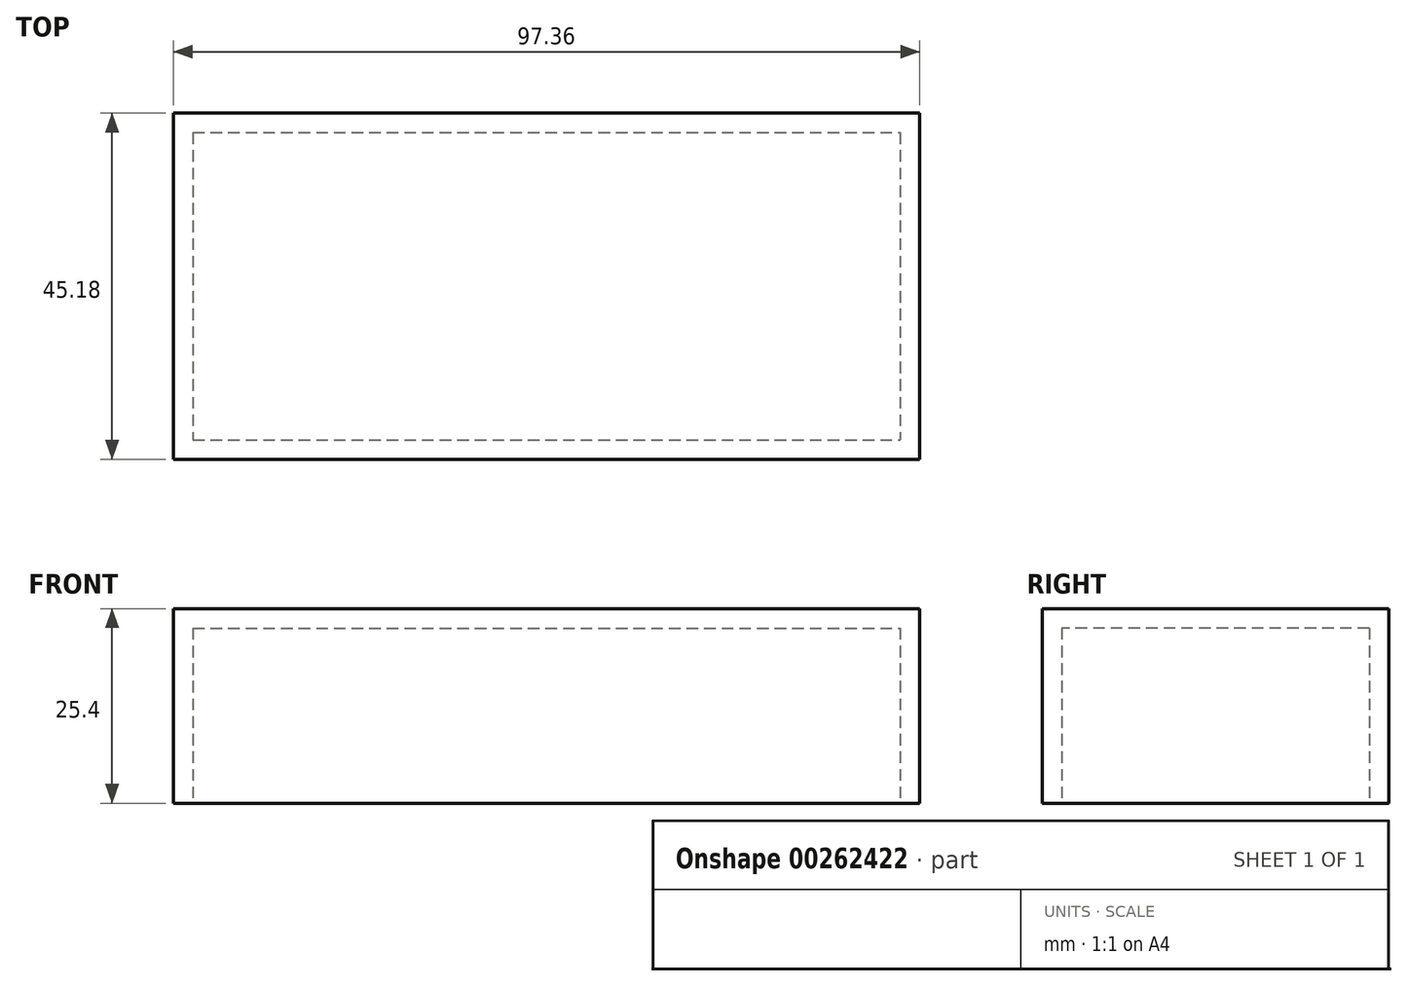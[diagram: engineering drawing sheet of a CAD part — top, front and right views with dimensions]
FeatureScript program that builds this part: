
annotation { "Feature Type Name" : "Feature", "Feature Type Description" : "" }
export const myFeature = defineFeature(function(context is Context, id is Id, definition is map)
    precondition{}
    {
        {
            var Q0;
            Q0=qCreatedBy(makeId("Top.planeOp"),FACE);
            var sketch = newSketch(context, id + "F0", { "sketchPlane" : qUnion([Q0])});
            skLineSegment(sketch, "E0.bottom", {"start": v(-46.93, 22.59) * mm, "end": v(50.43, 22.59) * mm});
            skLineSegment(sketch, "E0.top", {"start": v(-46.93, -22.59) * mm, "end": v(50.43, -22.59) * mm});
            skLineSegment(sketch, "E0.left", {"start": v(-46.93, 22.59) * mm, "end": v(-46.93, -22.59) * mm});
            skLineSegment(sketch, "E0.right", {"start": v(50.43, 22.59) * mm, "end": v(50.43, -22.59) * mm});
            skSolve(sketch);
        }
        {
            var Q0;
            Q0=qCreatedBy(makeId("Top.planeOp"),FACE);
            var sketch = newSketch(context, id + "F1", { "sketchPlane" : qUnion([Q0])});
            skCircle(sketch, "E1", {"center": v(-31.77, 8.9) * mm, "radius": 7 * mm});
            skCircle(sketch, "E2", {"center": v(-4.96, 8.9) * mm, "radius": 7.96 * mm});
            skCircle(sketch, "E3", {"center": v(17.2, 9.47) * mm, "radius": 8.47 * mm});
            skCircle(sketch, "E4", {"center": v(38.77, 8.9) * mm, "radius": 8.21 * mm});
            skCircle(sketch, "E5", {"center": v(-38.18, -10.93) * mm, "radius": 5.74 * mm});
            skCircle(sketch, "E6", {"center": v(-21.28, -12.1) * mm, "radius": 5.83 * mm});
            skCircle(sketch, "E7", {"center": v(-4.96, -11.8) * mm, "radius": 7.58 * mm});
            skCircle(sketch, "E8", {"center": v(13.12, -13.55) * mm, "radius": 7.9 * mm});
            skCircle(sketch, "E9", {"center": v(36.73, -11.8) * mm, "radius": 8.92 * mm});
            skSolve(sketch);
        }
        {
            var Q0;
            Q0=makeQuery(id+"F0.imprint","IMPRINT",FACE,{"disambiguationData":[TD([[makeQuery(id+"F0.imprint","IMPRINT",EDGE,{"derivedFrom":sQuery(id+"F0.wireOp",EDGE,"E0.bottom")}),-1.0]])]});
            extrude(context, id + "F2", {"entities" : qUnion([Q0]), "depth" : 25.4 * mm});
        }
        {
            var Q0;
            Q0=sQuery(id+"F1.wireOp",EDGE,"E1");
            var Q1;
            Q1=sQuery(id+"F1.wireOp",EDGE,"E2");
            var Q2;
            Q2=sQuery(id+"F1.wireOp",EDGE,"E4");
            var Q3;
            Q3=sQuery(id+"F1.wireOp",EDGE,"E9");
            var Q4;
            Q4=sQuery(id+"F1.wireOp",EDGE,"E7");
            var Q5;
            Q5=sQuery(id+"F1.wireOp",EDGE,"E5");
            extrude(context, id + "F3", {"bodyType" : ToolBodyType.SURFACE, "surfaceEntities" : qUnion([Q0, Q1, Q2, Q3, Q4, Q5]), "depth" : 50.8 * mm});
        }
        {
            var Q0;
            Q0=makeQuery(id+"F2.opExtrude","CAP_FACE",FACE,{"disambiguationData":[OSD([sQuery(id+"F0.wireOp",EDGE,"E0.bottom"),sQuery(id+"F0.wireOp",EDGE,"E0.top"),sQuery(id+"F0.wireOp",EDGE,"E0.left"),sQuery(id+"F0.wireOp",EDGE,"E0.right")])],"isStart":true});
            shell(context, id + "F4", {"entities" : qUnion([Q0]), "thickness" : 2.54 * mm});
        }
    });
